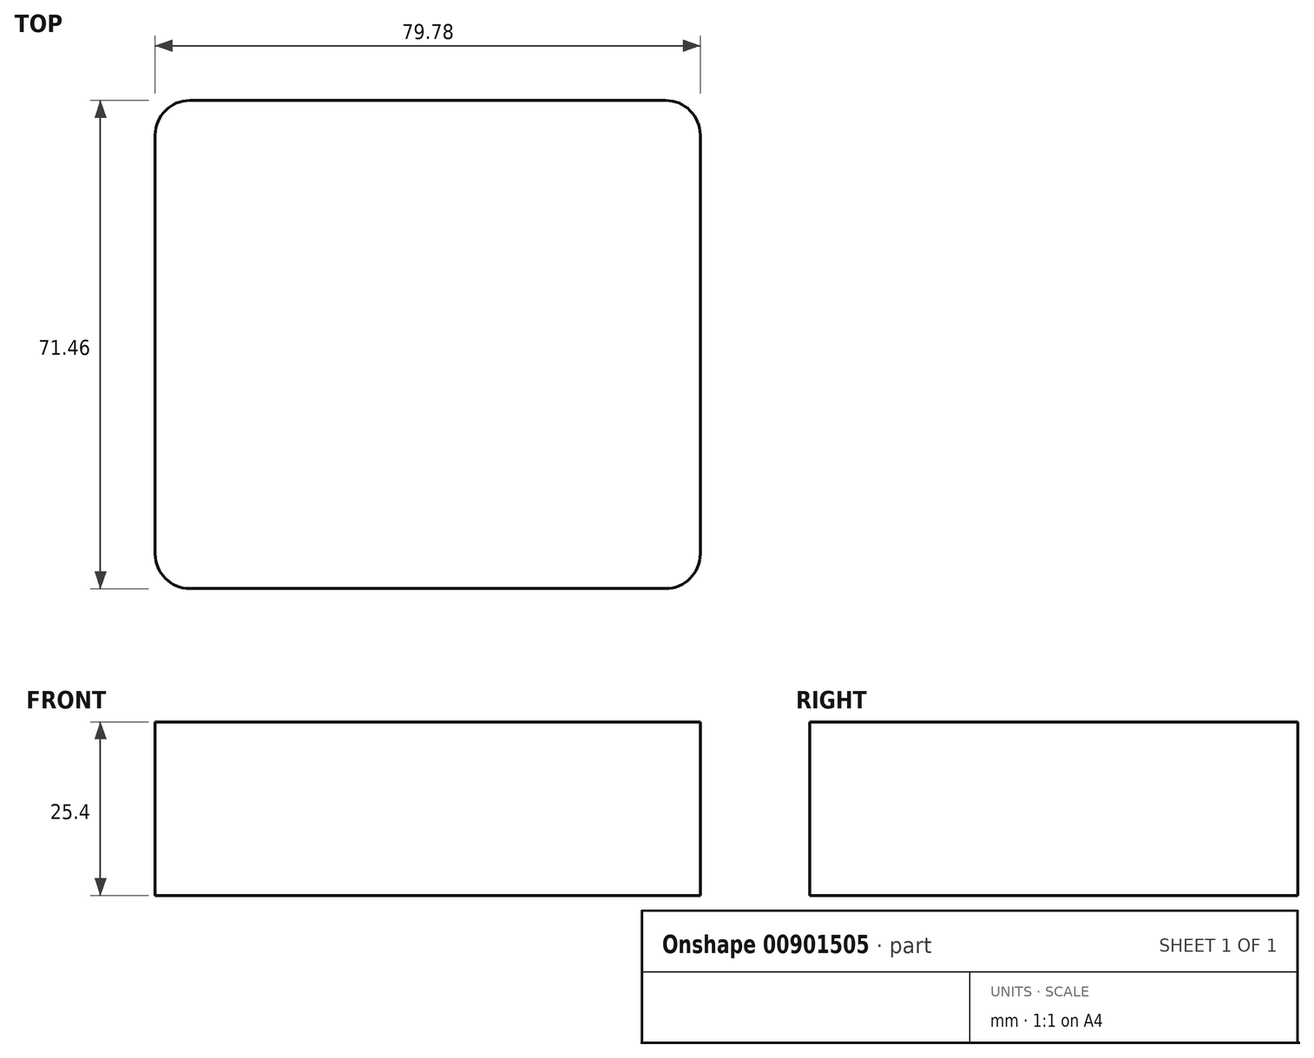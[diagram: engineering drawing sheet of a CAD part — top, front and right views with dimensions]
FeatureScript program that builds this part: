
annotation { "Feature Type Name" : "Feature", "Feature Type Description" : "" }
export const myFeature = defineFeature(function(context is Context, id is Id, definition is map)
    precondition{}
    {
        {
            var Q0;
            Q0=qCreatedBy(makeId("Top.planeOp"),FACE);
            var sketch = newSketch(context, id + "F0", { "sketchPlane" : qUnion([Q0])});
            skLineSegment(sketch, "E0.bottom", {"start": v(39.89, 35.73) * mm, "end": v(-39.89, 35.73) * mm});
            skLineSegment(sketch, "E0.top", {"start": v(39.89, -35.73) * mm, "end": v(-39.89, -35.73) * mm});
            skLineSegment(sketch, "E0.left", {"start": v(39.89, 35.73) * mm, "end": v(39.89, -35.73) * mm});
            skLineSegment(sketch, "E0.right", {"start": v(-39.89, 35.73) * mm, "end": v(-39.89, -35.73) * mm});
            skPoint(sketch, "E0.middle", {"position": v(0, 0) * mm});
            skSolve(sketch);
        }
        {
            var Q0;
            Q0 = qSketchRegion(id + "F0", true);
            extrude(context, id + "F1", {"entities" : qUnion([Q0]), "endBound" : BoundingType.SYMMETRIC, "depth" : 25.4 * mm, "offsetDistance" : 25.4 * mm});
        }
        {
            var Q0;
            Q0=makeQuery(id+"F1.opExtrude","SWEPT_EDGE",EDGE,{"disambiguationData":[OSD([sQuery(id+"F0.wireOp",EDGE,"E0.bottom"),sQuery(id+"F0.wireOp",EDGE,"E0.left")])]});
            var Q1;
            Q1=makeQuery(id+"F1.opExtrude","SWEPT_EDGE",EDGE,{"disambiguationData":[OSD([sQuery(id+"F0.wireOp",EDGE,"E0.bottom"),sQuery(id+"F0.wireOp",EDGE,"E0.right")])]});
            var Q2;
            Q2=makeQuery(id+"F1.opExtrude","SWEPT_EDGE",EDGE,{"disambiguationData":[OSD([sQuery(id+"F0.wireOp",EDGE,"E0.top"),sQuery(id+"F0.wireOp",EDGE,"E0.right")])]});
            var Q3;
            Q3=makeQuery(id+"F1.opExtrude","SWEPT_EDGE",EDGE,{"disambiguationData":[OSD([sQuery(id+"F0.wireOp",EDGE,"E0.top"),sQuery(id+"F0.wireOp",EDGE,"E0.left")])]});
            fillet(context, id + "F2", {"entities" : qUnion([Q0, Q1, Q2, Q3]), "radius" : 5.08 * mm, "tangentPropagation" : true, "allowEdgeOverflow" : false});
        }
    });
